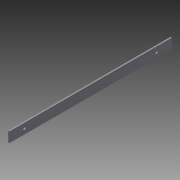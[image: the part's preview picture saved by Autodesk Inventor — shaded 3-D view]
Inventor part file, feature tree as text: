
AUTODESK INVENTOR PART (.ipt)
format: ipt  version: 2013 (Build 170138000, 138)  size: 81,408 bytes
history: native  units: in
note: dims shown in document units (in); Inventor stores cm internally (conversion verified against a paired STEP export)
features: extrude x2, sketch x2
ambient origin geometry x8: Origin, YZ Plane, XZ Plane, XY Plane, X Axis, Y Axis, Z Axis, Center Point
bodies: Solid1 (feature_tree)
feature tree (4):
  extrude  "Extrusion1"  Depth=16.0in
  extrude  "Extrusion2"  Depth=1.5in
  sketch  "Sketch1"  dims[d0=1.0in d1=16.0in]
  sketch  "Sketch2"  dims[d2=0.125in d3=0.0in d4=1.5in d5=0.0in d6=1.5in d7=180.0deg d8=0.25in d9=0.25in d10=0.125in d11=0.0in]
